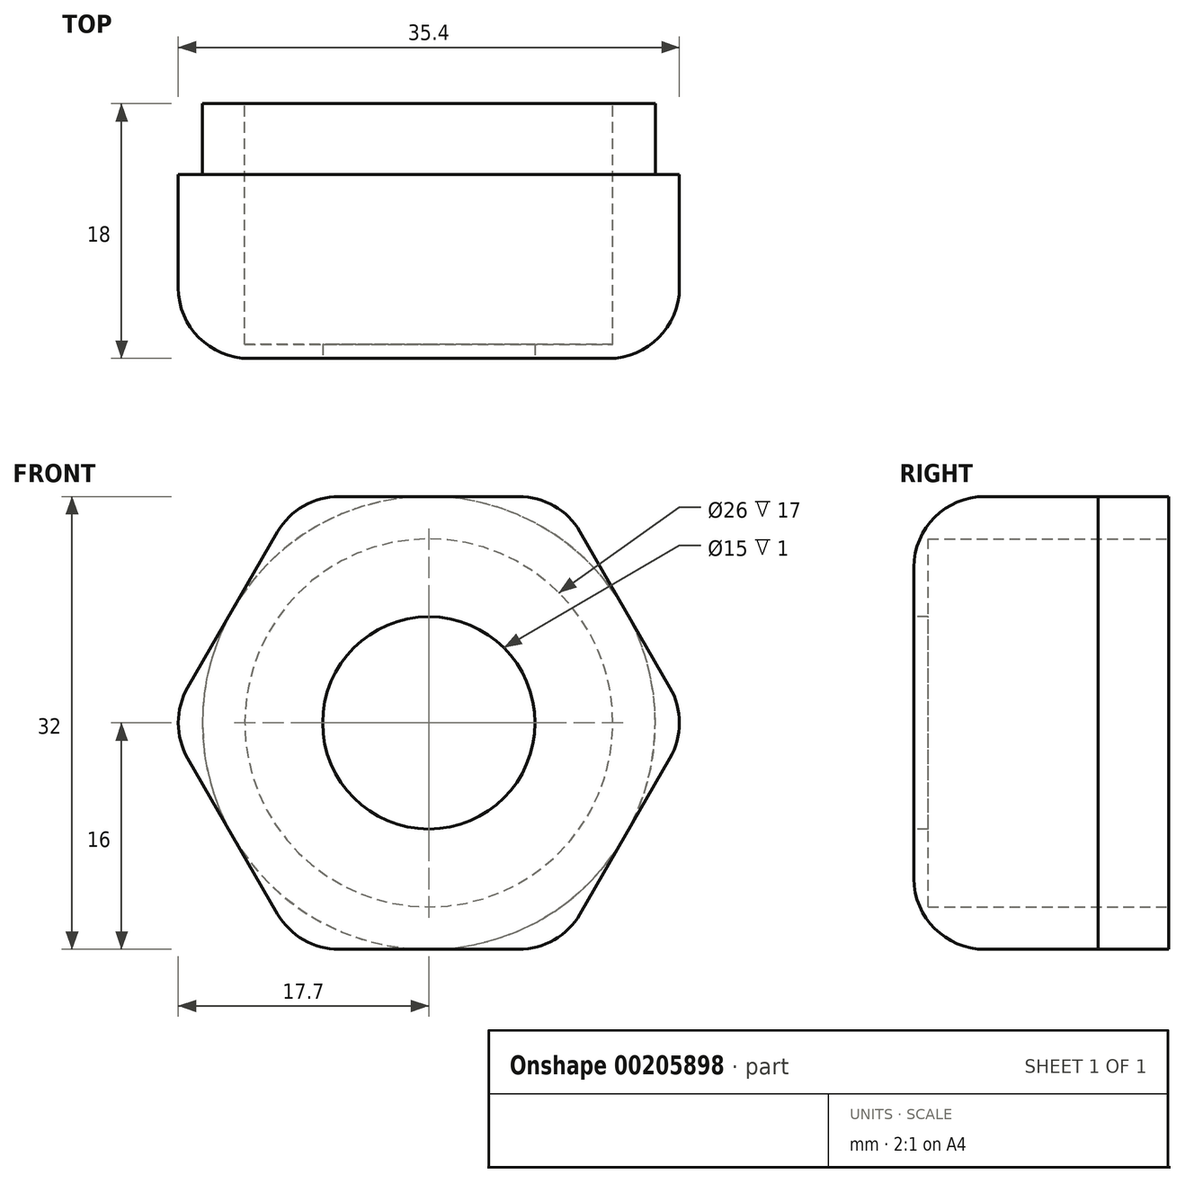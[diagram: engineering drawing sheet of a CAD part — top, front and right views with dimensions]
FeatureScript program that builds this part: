
annotation { "Feature Type Name" : "Feature", "Feature Type Description" : "" }
export const myFeature = defineFeature(function(context is Context, id is Id, definition is map)
    precondition{}
    {
        {
            var Q0;
            Q0=qCreatedBy(makeId("Front.planeOp"),FACE);
            var sketch = newSketch(context, id + "F0", { "sketchPlane" : qUnion([Q0])});
            skCircle(sketch, "E0", {"center": v(0, 0) * mm, "radius": 13 * mm});
            skCircle(sketch, "E1", {"center": v(0, 0) * mm, "radius": 16 * mm});
            skSolve(sketch);
        }
        {
            var Q0;
            Q0 = qSketchRegion(id + "F0", true);
            extrude(context, id + "F1", {"entities" : qUnion([Q0]), "depth" : 5 * mm});
        }
        {
            var Q0;
            Q0=makeQuery(id+"F1.opExtrude","CAP_FACE",FACE,{"disambiguationData":[OSD([sQuery(id+"F0.wireOp",EDGE,"E0"),sQuery(id+"F0.wireOp",EDGE,"E1")])],"isStart":false});
            var sketch = newSketch(context, id + "F2", { "sketchPlane" : qUnion([Q0])});
            skCircle(sketch, "E2.cCircle", {"center": v(0, 0) * mm, "radius": 16 * mm, "construction": true});
            skLineSegment(sketch, "E2.0", {"start": v(-6.35, 16) * mm, "end": v(6.35, 16) * mm});
            skLineSegment(sketch, "E2.1", {"start": v(10.68, 13.5) * mm, "end": v(17.03, 2.5) * mm});
            skLineSegment(sketch, "E2.2", {"start": v(17.03, -2.5) * mm, "end": v(10.68, -13.5) * mm});
            skLineSegment(sketch, "E2.3", {"start": v(6.35, -16) * mm, "end": v(-6.35, -16) * mm});
            skLineSegment(sketch, "E2.4", {"start": v(-10.68, -13.5) * mm, "end": v(-17.03, -2.5) * mm});
            skLineSegment(sketch, "E2.5", {"start": v(-17.03, 2.5) * mm, "end": v(-10.68, 13.5) * mm});
            skPoint(sketch, "E2.0.midPoint", {"position": v(0, 16) * mm});
            skPoint(sketch, "E3.visualSharp", {"position": v(-9.24, 16) * mm});
            skArc(sketch, "E3.filletArc", {"start": v(-6.35, 16) * mm, "mid": v(-8.85, 15.33) * mm, "end": v(-10.68, 13.5) * mm});
            skPoint(sketch, "E4.visualSharp", {"position": v(9.24, 16) * mm});
            skArc(sketch, "E4.filletArc", {"start": v(10.68, 13.5) * mm, "mid": v(8.85, 15.33) * mm, "end": v(6.35, 16) * mm});
            skPoint(sketch, "E5.visualSharp", {"position": v(18.48, 0) * mm});
            skArc(sketch, "E5.filletArc", {"start": v(17.03, -2.5) * mm, "mid": v(17.7, 0) * mm, "end": v(17.03, 2.5) * mm});
            skPoint(sketch, "E6.visualSharp", {"position": v(9.24, -16) * mm});
            skArc(sketch, "E6.filletArc", {"start": v(6.35, -16) * mm, "mid": v(8.85, -15.33) * mm, "end": v(10.68, -13.5) * mm});
            skPoint(sketch, "E7.visualSharp", {"position": v(-9.24, -16) * mm});
            skArc(sketch, "E7.filletArc", {"start": v(-10.68, -13.5) * mm, "mid": v(-8.85, -15.33) * mm, "end": v(-6.35, -16) * mm});
            skPoint(sketch, "E8.visualSharp", {"position": v(-18.48, 0) * mm});
            skArc(sketch, "E8.filletArc", {"start": v(-17.03, 2.5) * mm, "mid": v(-17.7, 0) * mm, "end": v(-17.03, -2.5) * mm});
            skCircle(sketch, "E9", {"center": v(0, 0) * mm, "radius": 13 * mm});
            skSolve(sketch);
        }
        {
            var Q0;
            Q0 = qSketchRegion(id + "F2", true);
            extrude(context, id + "F3", {"entities" : qUnion([Q0]), "operationType" : NewBodyOperationType.ADD, "depth" : 13 * mm});
        }
        {
            var Q0;
            Q0=makeQuery(id+"F3.opExtrude","CAP_FACE",FACE,{"disambiguationData":[OSD([sQuery(id+"F2.wireOp",EDGE,"E2.0"),sQuery(id+"F2.wireOp",EDGE,"E2.1"),sQuery(id+"F2.wireOp",EDGE,"E2.2"),sQuery(id+"F2.wireOp",EDGE,"E2.3"),sQuery(id+"F2.wireOp",EDGE,"E2.4"),sQuery(id+"F2.wireOp",EDGE,"E2.5"),sQuery(id+"F2.wireOp",EDGE,"E3.filletArc"),sQuery(id+"F2.wireOp",EDGE,"E4.filletArc"),sQuery(id+"F2.wireOp",EDGE,"E5.filletArc"),sQuery(id+"F2.wireOp",EDGE,"E6.filletArc"),sQuery(id+"F2.wireOp",EDGE,"E7.filletArc"),sQuery(id+"F2.wireOp",EDGE,"E8.filletArc"),sQuery(id+"F2.wireOp",EDGE,"E9")])],"isStart":false});
            var sketch = newSketch(context, id + "F4", { "sketchPlane" : qUnion([Q0])});
            skCircle(sketch, "E10.cCircle", {"center": v(0, 0) * mm, "radius": 16 * mm, "construction": true});
            skLineSegment(sketch, "E10.0", {"start": v(-6.35, 16) * mm, "end": v(6.35, 16) * mm});
            skLineSegment(sketch, "E10.1", {"start": v(10.68, 13.5) * mm, "end": v(17.03, 2.5) * mm});
            skLineSegment(sketch, "E10.2", {"start": v(17.03, -2.5) * mm, "end": v(10.68, -13.5) * mm});
            skLineSegment(sketch, "E10.3", {"start": v(6.35, -16) * mm, "end": v(-6.35, -16) * mm});
            skLineSegment(sketch, "E10.4", {"start": v(-10.68, -13.5) * mm, "end": v(-17.03, -2.5) * mm});
            skLineSegment(sketch, "E10.5", {"start": v(-17.03, 2.5) * mm, "end": v(-10.68, 13.5) * mm});
            skPoint(sketch, "E10.0.midPoint", {"position": v(0, 16) * mm});
            skPoint(sketch, "E11.visualSharp", {"position": v(-9.24, 16) * mm});
            skArc(sketch, "E11.filletArc", {"start": v(-6.35, 16) * mm, "mid": v(-8.85, 15.33) * mm, "end": v(-10.68, 13.5) * mm});
            skPoint(sketch, "E12.visualSharp", {"position": v(9.24, 16) * mm});
            skArc(sketch, "E12.filletArc", {"start": v(10.68, 13.5) * mm, "mid": v(8.85, 15.33) * mm, "end": v(6.35, 16) * mm});
            skPoint(sketch, "E13.visualSharp", {"position": v(18.48, 0) * mm});
            skArc(sketch, "E13.filletArc", {"start": v(17.03, -2.5) * mm, "mid": v(17.7, 0) * mm, "end": v(17.03, 2.5) * mm});
            skPoint(sketch, "E14.visualSharp", {"position": v(9.24, -16) * mm});
            skArc(sketch, "E14.filletArc", {"start": v(6.35, -16) * mm, "mid": v(8.85, -15.33) * mm, "end": v(10.68, -13.5) * mm});
            skPoint(sketch, "E15.visualSharp", {"position": v(-9.24, -16) * mm});
            skArc(sketch, "E15.filletArc", {"start": v(-10.68, -13.5) * mm, "mid": v(-8.85, -15.33) * mm, "end": v(-6.35, -16) * mm});
            skPoint(sketch, "E16.visualSharp", {"position": v(-18.48, 0) * mm});
            skArc(sketch, "E16.filletArc", {"start": v(-17.03, 2.5) * mm, "mid": v(-17.7, 0) * mm, "end": v(-17.03, -2.5) * mm});
            skCircle(sketch, "E17", {"center": v(0, 0) * mm, "radius": 7.5 * mm});
            skSolve(sketch);
        }
        {
            var Q0;
            Q0 = qSketchRegion(id + "F4", true);
            extrude(context, id + "F5", {"entities" : qUnion([Q0]), "operationType" : NewBodyOperationType.ADD, "oppositeDirection" : true, "depth" : 1 * mm});
        }
        {
            var Q0;
            Q0=makeQuery(id+"F3.opExtrude","CAP_EDGE",EDGE,{"disambiguationData":[OSD([sQuery(id+"F2.wireOp",EDGE,"E2.1")])],"isStart":false});
            fillet(context, id + "F6", {"entities" : qUnion([Q0]), "radius" : 5 * mm, "tangentPropagation" : true, "allowEdgeOverflow" : false});
        }
    });
